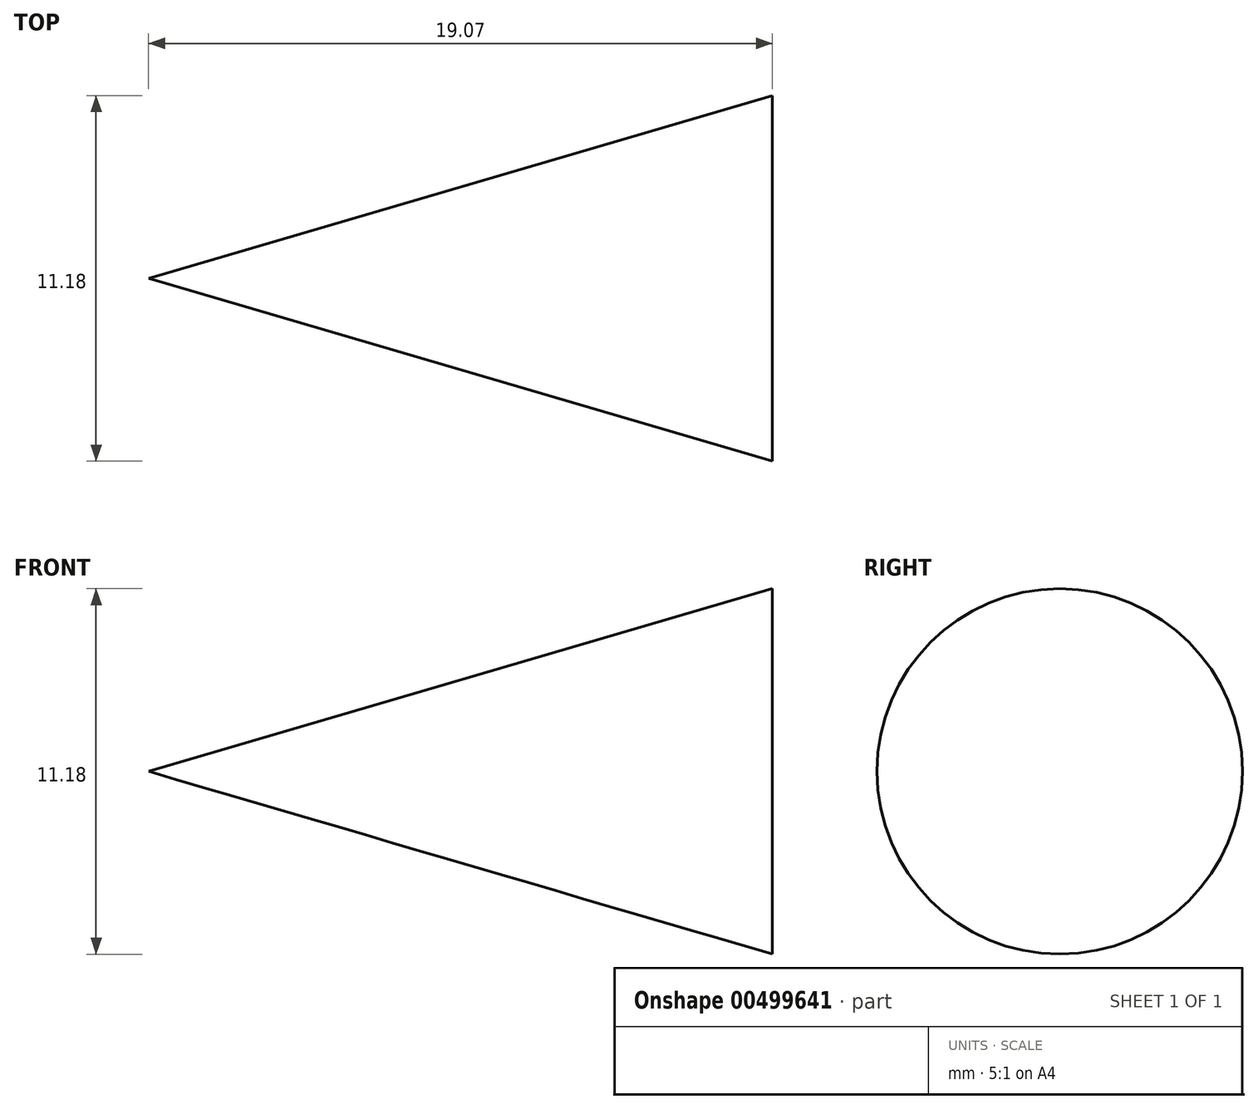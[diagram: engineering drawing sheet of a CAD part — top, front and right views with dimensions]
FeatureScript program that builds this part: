
annotation { "Feature Type Name" : "Feature", "Feature Type Description" : "" }
export const myFeature = defineFeature(function(context is Context, id is Id, definition is map)
    precondition{}
    {
        {
            var Q0;
            Q0=qCreatedBy(makeId("Front.planeOp"),FACE);
            var sketch = newSketch(context, id + "F0", { "sketchPlane" : qUnion([Q0])});
            skLineSegment(sketch, "E0", {"start": v(0, 0) * mm, "end": v(-9.53, 0) * mm});
            skLineSegment(sketch, "E1", {"start": v(-9.53, 0) * mm, "end": v(9.53, 0) * mm});
            skLineSegment(sketch, "E2", {"start": v(-9.52, 0) * mm, "end": v(9.54, 5.59) * mm});
            skLineSegment(sketch, "E3", {"start": v(9.54, 5.59) * mm, "end": v(9.53, 0) * mm});
            skSolve(sketch);
        }
        {
            var Q0;
            {var subQ0=sQuery(id+"F0.wireOp",EDGE,"E2");Q0=makeQuery(id+"F0.imprint","IMPRINT",FACE,{"disambiguationData":[TD([[makeQuery(id+"F0.imprint","IMPRINT",EDGE,{"derivedFrom":subQ0}),-1.0]])]});}
            var Q1;
            Q1=sQuery(id+"F0.wireOp",EDGE,"E1");
            revolve(context, id + "F1", {"entities" : qUnion([Q0]), "axis" : qUnion([Q1]), "revolveType" : RevolveType.FULL});
        }
    });
